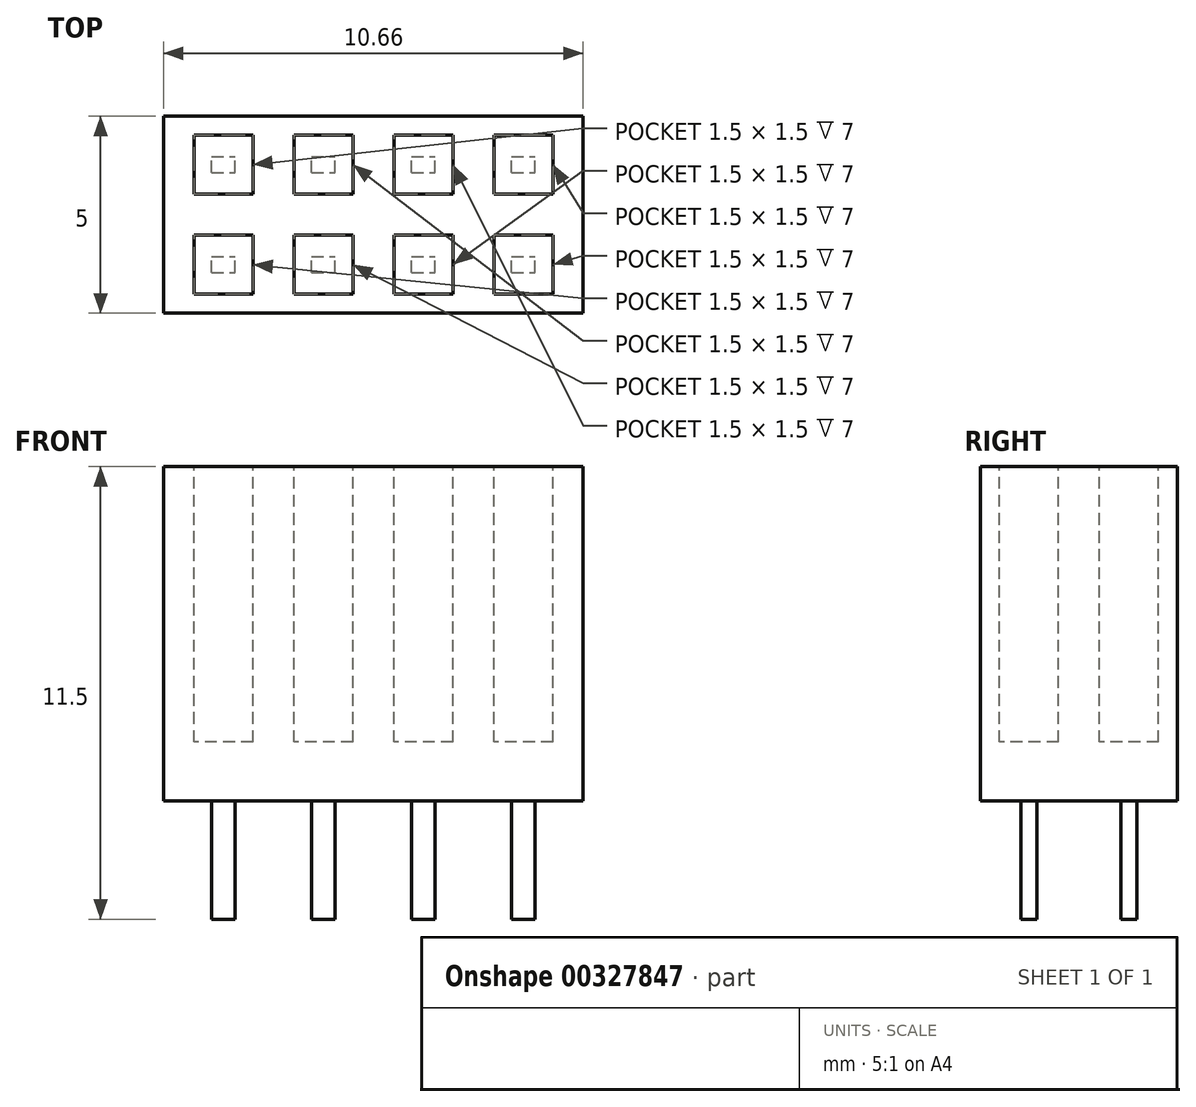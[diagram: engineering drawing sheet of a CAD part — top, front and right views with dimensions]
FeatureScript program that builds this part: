
annotation { "Feature Type Name" : "Feature", "Feature Type Description" : "" }
export const myFeature = defineFeature(function(context is Context, id is Id, definition is map)
    precondition{}
    {
        {
            var Q0;
            Q0=qCreatedBy(makeId("Top.planeOp"),FACE);
            var sketch = newSketch(context, id + "F0", { "sketchPlane" : qUnion([Q0])});
            skLineSegment(sketch, "E0.bottom", {"start": v(-5.33, 2.5) * mm, "end": v(5.33, 2.5) * mm});
            skLineSegment(sketch, "E0.top", {"start": v(-5.33, -2.5) * mm, "end": v(5.33, -2.5) * mm});
            skLineSegment(sketch, "E0.left", {"start": v(-5.33, 2.5) * mm, "end": v(-5.33, -2.5) * mm});
            skLineSegment(sketch, "E0.right", {"start": v(5.33, 2.5) * mm, "end": v(5.33, -2.5) * mm});
            skPoint(sketch, "E0.middle", {"position": v(0, 0) * mm});
            skSolve(sketch);
        }
        {
            var Q0;
            Q0=qSketchRegion(id+"F0",true);
            extrude(context, id + "F1", {"entities" : qUnion([Q0]), "depth" : 8.5 * mm});
        }
        {
            var Q0;
            Q0=makeQuery(id+"F1.opExtrude","CAP_FACE",FACE,{"disambiguationData":[OSD([sQuery(id+"F0.wireOp",EDGE,"E0.bottom"),sQuery(id+"F0.wireOp",EDGE,"E0.top"),sQuery(id+"F0.wireOp",EDGE,"E0.left"),sQuery(id+"F0.wireOp",EDGE,"E0.right")])],"isStart":false});
            var sketch = newSketch(context, id + "F2", { "sketchPlane" : qUnion([Q0])});
            skLineSegment(sketch, "E1.bottom", {"start": v(-3.06, 2.02) * mm, "end": v(-4.56, 2.02) * mm});
            skLineSegment(sketch, "E1.top", {"start": v(-3.06, 0.52) * mm, "end": v(-4.56, 0.52) * mm});
            skLineSegment(sketch, "E1.left", {"start": v(-3.06, 2.02) * mm, "end": v(-3.06, 0.52) * mm});
            skLineSegment(sketch, "E1.right", {"start": v(-4.56, 2.02) * mm, "end": v(-4.56, 0.52) * mm});
            skPoint(sketch, "E1.middle", {"position": v(-3.8, 1.27) * mm});
            skLineSegment(sketch, "E2.0.1.0", {"start": v(-3.06, -0.52) * mm, "end": v(-4.56, -0.52) * mm});
            skLineSegment(sketch, "E2.0.1.1", {"start": v(-3.06, -0.52) * mm, "end": v(-3.06, -2.02) * mm});
            skLineSegment(sketch, "E2.0.1.2", {"start": v(-4.56, -0.52) * mm, "end": v(-4.56, -2.02) * mm});
            skLineSegment(sketch, "E2.0.1.3", {"start": v(-3.06, -2.02) * mm, "end": v(-4.56, -2.02) * mm});
            skLineSegment(sketch, "E2.1.0.0", {"start": v(-0.52, 2.02) * mm, "end": v(-2.02, 2.02) * mm});
            skLineSegment(sketch, "E2.1.0.1", {"start": v(-0.52, 2.02) * mm, "end": v(-0.52, 0.52) * mm});
            skLineSegment(sketch, "E2.1.0.2", {"start": v(-2.02, 2.02) * mm, "end": v(-2.02, 0.52) * mm});
            skLineSegment(sketch, "E2.1.0.3", {"start": v(-0.52, 0.52) * mm, "end": v(-2.02, 0.52) * mm});
            skLineSegment(sketch, "E2.1.1.0", {"start": v(-0.52, -0.52) * mm, "end": v(-2.02, -0.52) * mm});
            skLineSegment(sketch, "E2.1.1.1", {"start": v(-0.52, -0.52) * mm, "end": v(-0.52, -2.02) * mm});
            skLineSegment(sketch, "E2.1.1.2", {"start": v(-2.02, -0.52) * mm, "end": v(-2.02, -2.02) * mm});
            skLineSegment(sketch, "E2.1.1.3", {"start": v(-0.52, -2.02) * mm, "end": v(-2.02, -2.02) * mm});
            skLineSegment(sketch, "E2.2.0.0", {"start": v(2.02, 2.02) * mm, "end": v(0.52, 2.02) * mm});
            skLineSegment(sketch, "E2.2.0.1", {"start": v(2.02, 2.02) * mm, "end": v(2.02, 0.52) * mm});
            skLineSegment(sketch, "E2.2.0.2", {"start": v(0.52, 2.02) * mm, "end": v(0.52, 0.52) * mm});
            skLineSegment(sketch, "E2.2.0.3", {"start": v(2.02, 0.52) * mm, "end": v(0.52, 0.52) * mm});
            skLineSegment(sketch, "E2.2.1.0", {"start": v(2.02, -0.52) * mm, "end": v(0.52, -0.52) * mm});
            skLineSegment(sketch, "E2.2.1.1", {"start": v(2.02, -0.52) * mm, "end": v(2.02, -2.02) * mm});
            skLineSegment(sketch, "E2.2.1.2", {"start": v(0.52, -0.52) * mm, "end": v(0.52, -2.02) * mm});
            skLineSegment(sketch, "E2.2.1.3", {"start": v(2.02, -2.02) * mm, "end": v(0.52, -2.02) * mm});
            skLineSegment(sketch, "E2.3.0.0", {"start": v(4.56, 2.02) * mm, "end": v(3.06, 2.02) * mm});
            skLineSegment(sketch, "E2.3.0.1", {"start": v(4.56, 2.02) * mm, "end": v(4.56, 0.52) * mm});
            skLineSegment(sketch, "E2.3.0.2", {"start": v(3.06, 2.02) * mm, "end": v(3.06, 0.52) * mm});
            skLineSegment(sketch, "E2.3.0.3", {"start": v(4.56, 0.52) * mm, "end": v(3.06, 0.52) * mm});
            skLineSegment(sketch, "E2.3.1.0", {"start": v(4.56, -0.52) * mm, "end": v(3.06, -0.52) * mm});
            skLineSegment(sketch, "E2.3.1.1", {"start": v(4.56, -0.52) * mm, "end": v(4.56, -2.02) * mm});
            skLineSegment(sketch, "E2.3.1.2", {"start": v(3.06, -0.52) * mm, "end": v(3.06, -2.02) * mm});
            skLineSegment(sketch, "E2.3.1.3", {"start": v(4.56, -2.02) * mm, "end": v(3.06, -2.02) * mm});
            skLineSegment(sketch, "E2.4.0.0", {"start": v(7.1, 2.02) * mm, "end": v(5.6, 2.02) * mm});
            skLineSegment(sketch, "E2.4.0.1", {"start": v(7.1, 2.02) * mm, "end": v(7.1, 0.52) * mm});
            skLineSegment(sketch, "E2.4.0.2", {"start": v(5.6, 2.02) * mm, "end": v(5.6, 0.52) * mm});
            skLineSegment(sketch, "E2.4.0.3", {"start": v(7.1, 0.52) * mm, "end": v(5.6, 0.52) * mm});
            skLineSegment(sketch, "E2.4.1.0", {"start": v(7.1, -0.52) * mm, "end": v(5.6, -0.52) * mm});
            skLineSegment(sketch, "E2.4.1.1", {"start": v(7.1, -0.52) * mm, "end": v(7.1, -2.02) * mm});
            skLineSegment(sketch, "E2.4.1.2", {"start": v(5.6, -0.52) * mm, "end": v(5.6, -2.02) * mm});
            skLineSegment(sketch, "E2.4.1.3", {"start": v(7.1, -2.02) * mm, "end": v(5.6, -2.02) * mm});
            skLineSegment(sketch, "E2.5.0.0", {"start": v(9.64, 2.02) * mm, "end": v(8.14, 2.02) * mm});
            skLineSegment(sketch, "E2.5.0.1", {"start": v(9.64, 2.02) * mm, "end": v(9.64, 0.52) * mm});
            skLineSegment(sketch, "E2.5.0.2", {"start": v(8.14, 2.02) * mm, "end": v(8.14, 0.52) * mm});
            skLineSegment(sketch, "E2.5.0.3", {"start": v(9.64, 0.52) * mm, "end": v(8.14, 0.52) * mm});
            skLineSegment(sketch, "E2.5.1.0", {"start": v(9.64, -0.52) * mm, "end": v(8.14, -0.52) * mm});
            skLineSegment(sketch, "E2.5.1.1", {"start": v(9.64, -0.52) * mm, "end": v(9.64, -2.02) * mm});
            skLineSegment(sketch, "E2.5.1.2", {"start": v(8.14, -0.52) * mm, "end": v(8.14, -2.02) * mm});
            skLineSegment(sketch, "E2.5.1.3", {"start": v(9.64, -2.02) * mm, "end": v(8.14, -2.02) * mm});
            skLineSegment(sketch, "E2.direction1", {"start": v(-4.56, 2.02) * mm, "end": v(-2.02, 2.02) * mm, "construction": true});
            skLineSegment(sketch, "E2.direction2", {"start": v(-4.56, 2.02) * mm, "end": v(-4.56, -0.52) * mm, "construction": true});
            skSolve(sketch);
        }
        {
            var Q0;
            Q0=qSketchRegion(id+"F2",true);
            extrude(context, id + "F3", {"entities" : qUnion([Q0]), "operationType" : NewBodyOperationType.REMOVE, "oppositeDirection" : true, "depth" : 7 * mm});
        }
        {
            var Q0;
            Q0=makeQuery(id+"F1.opExtrude","CAP_FACE",FACE,{"disambiguationData":[OSD([sQuery(id+"F0.wireOp",EDGE,"E0.bottom"),sQuery(id+"F0.wireOp",EDGE,"E0.top"),sQuery(id+"F0.wireOp",EDGE,"E0.left"),sQuery(id+"F0.wireOp",EDGE,"E0.right")])],"isStart":true});
            var sketch = newSketch(context, id + "F4", { "sketchPlane" : qUnion([Q0])});
            skLineSegment(sketch, "E3.bottom", {"start": v(-4.1, 1.47) * mm, "end": v(-3.5, 1.47) * mm});
            skLineSegment(sketch, "E3.top", {"start": v(-4.1, 1.07) * mm, "end": v(-3.5, 1.07) * mm});
            skLineSegment(sketch, "E3.left", {"start": v(-4.1, 1.47) * mm, "end": v(-4.1, 1.07) * mm});
            skLineSegment(sketch, "E3.right", {"start": v(-3.5, 1.47) * mm, "end": v(-3.5, 1.07) * mm});
            skPoint(sketch, "E3.middle", {"position": v(-3.8, 1.27) * mm});
            skPoint(sketch, "E4.0", {"position": v(-4.56, 2.02) * mm});
            skPoint(sketch, "E4.1", {"position": v(-3.06, 0.52) * mm});
            skLineSegment(sketch, "E5", {"start": v(-4.56, 2.02) * mm, "end": v(-3.06, 0.52) * mm, "construction": true});
            skLineSegment(sketch, "E6.0.1.0", {"start": v(-4.1, -1.07) * mm, "end": v(-3.5, -1.07) * mm});
            skLineSegment(sketch, "E6.0.1.1", {"start": v(-4.1, -1.07) * mm, "end": v(-4.1, -1.47) * mm});
            skLineSegment(sketch, "E6.0.1.2", {"start": v(-4.1, -1.47) * mm, "end": v(-3.5, -1.47) * mm});
            skLineSegment(sketch, "E6.0.1.3", {"start": v(-3.5, -1.07) * mm, "end": v(-3.5, -1.47) * mm});
            skLineSegment(sketch, "E6.1.0.0", {"start": v(-1.57, 1.47) * mm, "end": v(-0.97, 1.47) * mm});
            skLineSegment(sketch, "E6.1.0.1", {"start": v(-1.57, 1.47) * mm, "end": v(-1.57, 1.07) * mm});
            skLineSegment(sketch, "E6.1.0.2", {"start": v(-1.57, 1.07) * mm, "end": v(-0.97, 1.07) * mm});
            skLineSegment(sketch, "E6.1.0.3", {"start": v(-0.97, 1.47) * mm, "end": v(-0.97, 1.07) * mm});
            skLineSegment(sketch, "E6.1.1.0", {"start": v(-1.57, -1.07) * mm, "end": v(-0.97, -1.07) * mm});
            skLineSegment(sketch, "E6.1.1.1", {"start": v(-1.57, -1.07) * mm, "end": v(-1.57, -1.47) * mm});
            skLineSegment(sketch, "E6.1.1.2", {"start": v(-1.57, -1.47) * mm, "end": v(-0.97, -1.47) * mm});
            skLineSegment(sketch, "E6.1.1.3", {"start": v(-0.97, -1.07) * mm, "end": v(-0.97, -1.47) * mm});
            skLineSegment(sketch, "E6.2.0.0", {"start": v(0.97, 1.47) * mm, "end": v(1.57, 1.47) * mm});
            skLineSegment(sketch, "E6.2.0.1", {"start": v(0.97, 1.47) * mm, "end": v(0.97, 1.07) * mm});
            skLineSegment(sketch, "E6.2.0.2", {"start": v(0.97, 1.07) * mm, "end": v(1.57, 1.07) * mm});
            skLineSegment(sketch, "E6.2.0.3", {"start": v(1.57, 1.47) * mm, "end": v(1.57, 1.07) * mm});
            skLineSegment(sketch, "E6.2.1.0", {"start": v(0.97, -1.07) * mm, "end": v(1.57, -1.07) * mm});
            skLineSegment(sketch, "E6.2.1.1", {"start": v(0.97, -1.07) * mm, "end": v(0.97, -1.47) * mm});
            skLineSegment(sketch, "E6.2.1.2", {"start": v(0.97, -1.47) * mm, "end": v(1.57, -1.47) * mm});
            skLineSegment(sketch, "E6.2.1.3", {"start": v(1.57, -1.07) * mm, "end": v(1.57, -1.47) * mm});
            skLineSegment(sketch, "E6.3.0.0", {"start": v(3.51, 1.47) * mm, "end": v(4.11, 1.47) * mm});
            skLineSegment(sketch, "E6.3.0.1", {"start": v(3.51, 1.47) * mm, "end": v(3.51, 1.07) * mm});
            skLineSegment(sketch, "E6.3.0.2", {"start": v(3.51, 1.07) * mm, "end": v(4.11, 1.07) * mm});
            skLineSegment(sketch, "E6.3.0.3", {"start": v(4.11, 1.47) * mm, "end": v(4.11, 1.07) * mm});
            skLineSegment(sketch, "E6.3.1.0", {"start": v(3.51, -1.07) * mm, "end": v(4.11, -1.07) * mm});
            skLineSegment(sketch, "E6.3.1.1", {"start": v(3.51, -1.07) * mm, "end": v(3.51, -1.47) * mm});
            skLineSegment(sketch, "E6.3.1.2", {"start": v(3.51, -1.47) * mm, "end": v(4.11, -1.47) * mm});
            skLineSegment(sketch, "E6.3.1.3", {"start": v(4.11, -1.07) * mm, "end": v(4.11, -1.47) * mm});
            skLineSegment(sketch, "E6.4.0.0", {"start": v(6.05, 1.47) * mm, "end": v(6.65, 1.47) * mm});
            skLineSegment(sketch, "E6.4.0.1", {"start": v(6.05, 1.47) * mm, "end": v(6.05, 1.07) * mm});
            skLineSegment(sketch, "E6.4.0.2", {"start": v(6.05, 1.07) * mm, "end": v(6.65, 1.07) * mm});
            skLineSegment(sketch, "E6.4.0.3", {"start": v(6.65, 1.47) * mm, "end": v(6.65, 1.07) * mm});
            skLineSegment(sketch, "E6.4.1.0", {"start": v(6.05, -1.07) * mm, "end": v(6.65, -1.07) * mm});
            skLineSegment(sketch, "E6.4.1.1", {"start": v(6.05, -1.07) * mm, "end": v(6.05, -1.47) * mm});
            skLineSegment(sketch, "E6.4.1.2", {"start": v(6.05, -1.47) * mm, "end": v(6.65, -1.47) * mm});
            skLineSegment(sketch, "E6.4.1.3", {"start": v(6.65, -1.07) * mm, "end": v(6.65, -1.47) * mm});
            skLineSegment(sketch, "E6.5.0.0", {"start": v(8.6, 1.47) * mm, "end": v(9.2, 1.47) * mm});
            skLineSegment(sketch, "E6.5.0.1", {"start": v(8.6, 1.47) * mm, "end": v(8.6, 1.07) * mm});
            skLineSegment(sketch, "E6.5.0.2", {"start": v(8.6, 1.07) * mm, "end": v(9.2, 1.07) * mm});
            skLineSegment(sketch, "E6.5.0.3", {"start": v(9.2, 1.47) * mm, "end": v(9.2, 1.07) * mm});
            skLineSegment(sketch, "E6.5.1.0", {"start": v(8.6, -1.07) * mm, "end": v(9.2, -1.07) * mm});
            skLineSegment(sketch, "E6.5.1.1", {"start": v(8.6, -1.07) * mm, "end": v(8.6, -1.47) * mm});
            skLineSegment(sketch, "E6.5.1.2", {"start": v(8.6, -1.47) * mm, "end": v(9.2, -1.47) * mm});
            skLineSegment(sketch, "E6.5.1.3", {"start": v(9.2, -1.07) * mm, "end": v(9.2, -1.47) * mm});
            skLineSegment(sketch, "E6.direction1", {"start": v(-4.1, 1.47) * mm, "end": v(-1.57, 1.47) * mm, "construction": true});
            skLineSegment(sketch, "E6.direction2", {"start": v(-4.1, 1.47) * mm, "end": v(-4.1, -1.07) * mm, "construction": true});
            skSolve(sketch);
        }
        {
            var Q0;
            Q0=qSketchRegion(id+"F4",true);
            extrude(context, id + "F5", {"entities" : qUnion([Q0]), "depth" : 3 * mm});
        }
        {
            var Q0;
            Q0=makeQuery(id+"F5.opExtrude","SWEPT_BODY",BODY,{"disambiguationData":[OSD([sQuery(id+"F4.wireOp",EDGE,"E6.5.1.0"),sQuery(id+"F4.wireOp",EDGE,"E6.5.1.1"),sQuery(id+"F4.wireOp",EDGE,"E6.5.1.2"),sQuery(id+"F4.wireOp",EDGE,"E6.5.1.3")])]});
            var Q1;
            Q1=makeQuery(id+"F5.opExtrude","SWEPT_BODY",BODY,{"disambiguationData":[OSD([sQuery(id+"F4.wireOp",EDGE,"E6.5.0.0"),sQuery(id+"F4.wireOp",EDGE,"E6.5.0.1"),sQuery(id+"F4.wireOp",EDGE,"E6.5.0.2"),sQuery(id+"F4.wireOp",EDGE,"E6.5.0.3")])]});
            var Q2;
            Q2=makeQuery(id+"F5.opExtrude","SWEPT_BODY",BODY,{"disambiguationData":[OSD([sQuery(id+"F4.wireOp",EDGE,"E6.4.1.0"),sQuery(id+"F4.wireOp",EDGE,"E6.4.1.1"),sQuery(id+"F4.wireOp",EDGE,"E6.4.1.2"),sQuery(id+"F4.wireOp",EDGE,"E6.4.1.3")])]});
            var Q3;
            Q3=makeQuery(id+"F5.opExtrude","SWEPT_BODY",BODY,{"disambiguationData":[OSD([sQuery(id+"F4.wireOp",EDGE,"E6.4.0.0"),sQuery(id+"F4.wireOp",EDGE,"E6.4.0.1"),sQuery(id+"F4.wireOp",EDGE,"E6.4.0.2"),sQuery(id+"F4.wireOp",EDGE,"E6.4.0.3")])]});
            deleteBodies(context, id + "F6", {"entities" : qUnion([Q0, Q1, Q2, Q3])});
        }
    });
